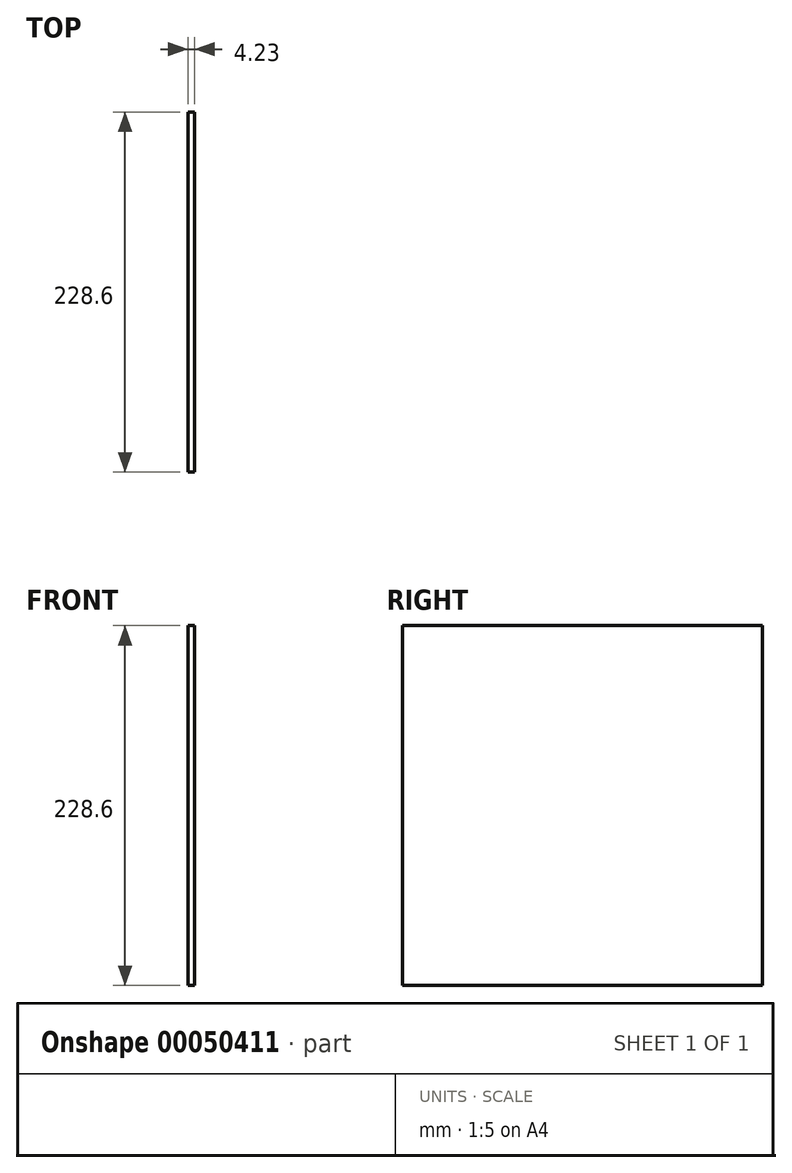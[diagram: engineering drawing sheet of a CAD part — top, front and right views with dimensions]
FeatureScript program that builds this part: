
annotation { "Feature Type Name" : "Feature", "Feature Type Description" : "" }
export const myFeature = defineFeature(function(context is Context, id is Id, definition is map)
    precondition{}
    {
        {
            var Q0;
            Q0=qCreatedBy(makeId("Right.planeOp"),FACE);
            var sketch = newSketch(context, id + "F0", { "sketchPlane" : qUnion([Q0])});
            skLineSegment(sketch, "E0.bottom", {"start": v(0, 0) * mm, "end": v(228.6, 0) * mm});
            skLineSegment(sketch, "E0.top", {"start": v(0, 228.6) * mm, "end": v(228.6, 228.6) * mm});
            skLineSegment(sketch, "E0.left", {"start": v(0, 0) * mm, "end": v(0, 228.6) * mm});
            skLineSegment(sketch, "E0.right", {"start": v(228.6, 0) * mm, "end": v(228.6, 228.6) * mm});
            skSolve(sketch);
        }
        {
            var Q0;
            Q0=makeQuery(id+"F0.imprint","IMPRINT",FACE,{"disambiguationData":[TD([[makeQuery(id+"F0.imprint","IMPRINT",EDGE,{"derivedFrom":sQuery(id+"F0.wireOp",EDGE,"E0.bottom")}),1.0]])]});
            extrude(context, id + "F1", {"entities" : qUnion([Q0]), "depth" : 4.23 * mm});
        }
    });
